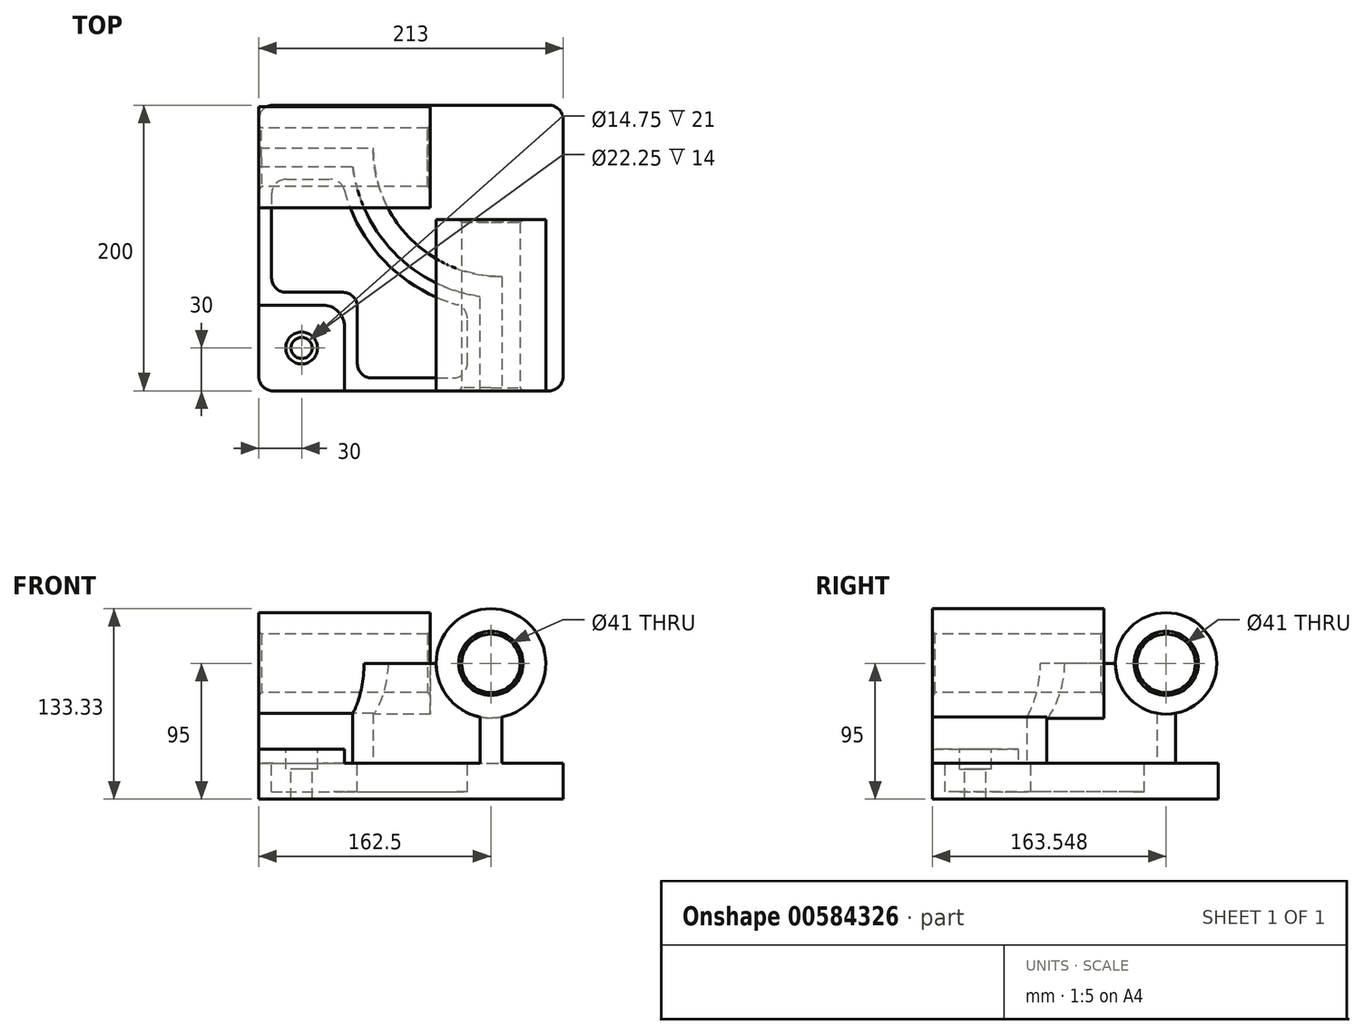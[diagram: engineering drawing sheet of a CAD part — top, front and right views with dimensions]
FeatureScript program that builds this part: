
annotation { "Feature Type Name" : "Feature", "Feature Type Description" : "" }
export const myFeature = defineFeature(function(context is Context, id is Id, definition is map)
    precondition{}
    {
        {
            var Q0;
            Q0=qCreatedBy(makeId("Top.planeOp"),FACE);
            var sketch = newSketch(context, id + "F0", { "sketchPlane" : qUnion([Q0])});
            skLineSegment(sketch, "E0.bottom", {"start": v(-106.5, 100) * mm, "end": v(106.5, 100) * mm});
            skLineSegment(sketch, "E0.top", {"start": v(-106.5, -100) * mm, "end": v(106.5, -100) * mm});
            skLineSegment(sketch, "E0.left", {"start": v(-106.5, 100) * mm, "end": v(-106.5, -100) * mm});
            skLineSegment(sketch, "E0.right", {"start": v(106.5, 100) * mm, "end": v(106.5, -100) * mm});
            skPoint(sketch, "E0.middle", {"position": v(0, 0) * mm});
            skSolve(sketch);
        }
        {
            var Q0;
            Q0 = qSketchRegion(id + "F0", true);
            extrude(context, id + "F1", {"entities" : qUnion([Q0]), "depth" : 25 * mm, "offsetDistance" : 25 * mm});
        }
        {
            var Q0;
            Q0=makeQuery(id+"F1.opExtrude","CAP_FACE",FACE,{"disambiguationData":[OSD([sQuery(id+"F0.wireOp",EDGE,"E0.bottom"),sQuery(id+"F0.wireOp",EDGE,"E0.top"),sQuery(id+"F0.wireOp",EDGE,"E0.left"),sQuery(id+"F0.wireOp",EDGE,"E0.right")])],"isStart":false});
            var sketch = newSketch(context, id + "F2", { "sketchPlane" : qUnion([Q0])});
            skLineSegment(sketch, "E1.bottom", {"start": v(-106.5, -100) * mm, "end": v(-46.5, -100) * mm});
            skLineSegment(sketch, "E1.top", {"start": v(-106.5, -40) * mm, "end": v(-46.5, -40) * mm});
            skLineSegment(sketch, "E1.left", {"start": v(-106.5, -100) * mm, "end": v(-106.5, -40) * mm});
            skLineSegment(sketch, "E1.right", {"start": v(-46.5, -100) * mm, "end": v(-46.5, -40) * mm});
            skLineSegment(sketch, "E2", {"start": v(-97.5, 48.1) * mm, "end": v(-97.5, -31) * mm});
            skLineSegment(sketch, "E3", {"start": v(-97.5, -31) * mm, "end": v(-37.5, -31) * mm});
            skLineSegment(sketch, "E4", {"start": v(-37.5, -31) * mm, "end": v(-37.5, -91) * mm});
            skLineSegment(sketch, "E5", {"start": v(-37.5, -91) * mm, "end": v(39.5, -91) * mm});
            skLineSegment(sketch, "E6", {"start": v(-97.5, 48.1) * mm, "end": v(-48.38, 48.1) * mm});
            skLineSegment(sketch, "E7", {"start": v(-106.5, 57.1) * mm, "end": v(-40.7, 57.1) * mm});
            skLineSegment(sketch, "E8", {"start": v(-106.5, 70) * mm, "end": v(-26.5, 70) * mm});
            skLineSegment(sketch, "E9", {"start": v(-26.5, 70) * mm, "end": v(63.5, 70) * mm, "construction": true});
            skLineSegment(sketch, "E10", {"start": v(63.5, 70) * mm, "end": v(63.5, -20) * mm, "construction": true});
            skPoint(sketch, "E11", {"position": v(63.5, -20) * mm});
            skPoint(sketch, "E12", {"position": v(-26.5, 70) * mm});
            skLineSegment(sketch, "E13.0", {"start": v(106.5, 100) * mm, "end": v(106.5, -100) * mm});
            skLineSegment(sketch, "E14", {"start": v(93.5, -100) * mm, "end": v(93.5, 100) * mm});
            skArc(sketch, "E15", {"start": v(-26.5, 70) * mm, "mid": v(-0.14, 6.36) * mm, "end": v(63.5, -20) * mm});
            skArc(sketch, "E16", {"start": v(-40.7, 57.1) * mm, "mid": v(-11.5, -3.5) * mm, "end": v(48.5, -33.92) * mm});
            skLineSegment(sketch, "E17", {"start": v(63.5, -20) * mm, "end": v(63.5, -100) * mm});
            skPoint(sketch, "E18", {"position": v(-40.7, 57.1) * mm});
            skLineSegment(sketch, "E19", {"start": v(39.5, -91) * mm, "end": v(39.5, -41.45) * mm});
            skPoint(sketch, "E20", {"position": v(-48.38, 48.1) * mm});
            skPoint(sketch, "E21", {"position": v(39.5, -41.45) * mm});
            skArc(sketch, "E22.trimOffspring", {"start": v(-48.38, 48.1) * mm, "mid": v(-17.86, -9.85) * mm, "end": v(39.5, -41.45) * mm});
            skLineSegment(sketch, "E23", {"start": v(48.5, -100) * mm, "end": v(48.5, -33.92) * mm});
            skSolve(sketch);
        }
        {
            var Q0;
            Q0=makeQuery(id+"F2.imprint","IMPRINT",FACE,{"disambiguationData":[TD([[makeQuery(id+"F2.imprint","IMPRINT",EDGE,{"derivedFrom":sQuery(id+"F2.wireOp",EDGE,"E1.bottom")}),1.0]])]});
            extrude(context, id + "F3", {"entities" : qUnion([Q0]), "operationType" : NewBodyOperationType.ADD, "depth" : 10 * mm, "offsetDistance" : 25 * mm});
        }
        {
            var Q0;
            Q0=makeQuery(id+"F3.boolean.opBoolean","MERGE",EDGE,{"derivedFrom":[makeQuery(id+"F1.opExtrude","SWEPT_EDGE",EDGE,{"disambiguationData":[OSD([sQuery(id+"F0.wireOp",EDGE,"E0.top"),sQuery(id+"F0.wireOp",EDGE,"E0.left")])]}),makeQuery(id+"F3.opExtrude","SWEPT_EDGE",EDGE,{"disambiguationData":[OSD([sQuery(id+"F2.wireOp",EDGE,"E1.bottom"),sQuery(id+"F2.wireOp",EDGE,"E1.left")])]})]});
            var Q1;
            Q1=makeQuery(id+"F1.opExtrude","SWEPT_EDGE",EDGE,{"disambiguationData":[OSD([sQuery(id+"F0.wireOp",EDGE,"E0.top"),sQuery(id+"F0.wireOp",EDGE,"E0.right")])]});
            var Q2;
            Q2=makeQuery(id+"F1.opExtrude","SWEPT_EDGE",EDGE,{"disambiguationData":[OSD([sQuery(id+"F0.wireOp",EDGE,"E0.bottom"),sQuery(id+"F0.wireOp",EDGE,"E0.right")])]});
            var Q3;
            Q3=makeQuery(id+"F1.opExtrude","SWEPT_EDGE",EDGE,{"disambiguationData":[OSD([sQuery(id+"F0.wireOp",EDGE,"E0.bottom"),sQuery(id+"F0.wireOp",EDGE,"E0.left")])]});
            fillet(context, id + "F4", {"entities" : qUnion([Q0, Q1, Q2, Q3]), "radius" : 10 * mm, "tangentPropagation" : true, "allowEdgeOverflow" : false});
        }
        {
            var Q0;
            Q0=makeQuery(id+"F3.opExtrude","SWEPT_EDGE",EDGE,{"disambiguationData":[OSD([sQuery(id+"F2.wireOp",EDGE,"E1.top"),sQuery(id+"F2.wireOp",EDGE,"E1.right")])]});
            fillet(context, id + "F5", {"entities" : qUnion([Q0]), "radius" : 15 * mm, "tangentPropagation" : true, "allowEdgeOverflow" : false});
        }
        {
            var Q0;
            Q0=makeQuery(id+"F2.imprint","IMPRINT",FACE,{"disambiguationData":[TD([[makeQuery(id+"F2.imprint","IMPRINT",EDGE,{"derivedFrom":sQuery(id+"F2.wireOp",EDGE,"E2")}),1.0]])]});
            extrude(context, id + "F6", {"entities" : qUnion([Q0]), "operationType" : NewBodyOperationType.REMOVE, "oppositeDirection" : true, "depth" : 20 * mm, "offsetDistance" : 25 * mm});
        }
        {
            var Q0;
            {var subQ4=sQuery(id+"F2.wireOp",EDGE,"E7");Q0=makeQuery(id+"F2.imprint","IMPRINT",FACE,{"disambiguationData":[TD([[makeQuery(id+"F2.imprint","IMPRINT",EDGE,{"derivedFrom":subQ4}),1.0]])]});}
            extrude(context, id + "F7", {"entities" : qUnion([Q0]), "operationType" : NewBodyOperationType.ADD, "depth" : 70 * mm, "offsetDistance" : 25 * mm});
        }
        {
            var Q0;
            Q0=makeQuery(id+"F6.boolean.opBoolean","COPY",EDGE,{"derivedFrom":makeQuery(id+"F6.opExtrude","SWEPT_EDGE",EDGE,{"disambiguationData":[OSD([sQuery(id+"F2.wireOp",EDGE,"E6"),sQuery(id+"F2.wireOp",EDGE,"E22.trimOffspring")])]})});
            var Q1;
            Q1=makeQuery(id+"F6.boolean.opBoolean","COPY",EDGE,{"derivedFrom":makeQuery(id+"F6.opExtrude","SWEPT_EDGE",EDGE,{"disambiguationData":[OSD([sQuery(id+"F2.wireOp",EDGE,"E19"),sQuery(id+"F2.wireOp",EDGE,"E22.trimOffspring")])]})});
            var Q2;
            Q2=makeQuery(id+"F6.boolean.opBoolean","COPY",EDGE,{"derivedFrom":makeQuery(id+"F6.opExtrude","SWEPT_EDGE",EDGE,{"disambiguationData":[OSD([sQuery(id+"F2.wireOp",EDGE,"E3"),sQuery(id+"F2.wireOp",EDGE,"E4")])]})});
            var Q3;
            Q3=makeQuery(id+"F6.boolean.opBoolean","COPY",EDGE,{"derivedFrom":makeQuery(id+"F6.opExtrude","SWEPT_EDGE",EDGE,{"disambiguationData":[OSD([sQuery(id+"F2.wireOp",EDGE,"E2"),sQuery(id+"F2.wireOp",EDGE,"E6")])]})});
            var Q4;
            Q4=makeQuery(id+"F6.boolean.opBoolean","COPY",EDGE,{"derivedFrom":makeQuery(id+"F6.opExtrude","SWEPT_EDGE",EDGE,{"disambiguationData":[OSD([sQuery(id+"F2.wireOp",EDGE,"E5"),sQuery(id+"F2.wireOp",EDGE,"E19")])]})});
            var Q5;
            Q5=makeQuery(id+"F6.boolean.opBoolean","COPY",EDGE,{"derivedFrom":makeQuery(id+"F6.opExtrude","SWEPT_EDGE",EDGE,{"disambiguationData":[OSD([sQuery(id+"F2.wireOp",EDGE,"E4"),sQuery(id+"F2.wireOp",EDGE,"E5")])]})});
            var Q6;
            Q6=makeQuery(id+"F6.boolean.opBoolean","COPY",EDGE,{"derivedFrom":makeQuery(id+"F6.opExtrude","SWEPT_EDGE",EDGE,{"disambiguationData":[OSD([sQuery(id+"F2.wireOp",EDGE,"E2"),sQuery(id+"F2.wireOp",EDGE,"E3")])]})});
            fillet(context, id + "F8", {"entities" : qUnion([Q0, Q1, Q2, Q3, Q4, Q5, Q6]), "radius" : 10 * mm, "tangentPropagation" : true, "allowEdgeOverflow" : false});
        }
        {
            var Q0;
            Q0=makeQuery(id+"F7.opExtrude","SWEPT_FACE",FACE,{"disambiguationData":[OSD([sQuery(id+"F0.wireOp",EDGE,"E0.left")])]});
            var sketch = newSketch(context, id + "F9", { "sketchPlane" : qUnion([Q0])});
            skCircle(sketch, "E24", {"center": v(-63.55, 95) * mm, "radius": 35.5 * mm});
            skCircle(sketch, "E25", {"center": v(-63.55, 95) * mm, "radius": 20.5 * mm});
            skSolve(sketch);
        }
        {
            var Q0;
            {var subQ1=sQuery(id+"F0.wireOp",EDGE,"E0.left");var subQ6=makeQuery(id+"F7.opExtrude","CAP_EDGE",EDGE,{"disambiguationData":[OSD([subQ1])],"isStart":false});Q0=makeQuery(id+"F9.imprint","IMPRINT",FACE,{"disambiguationData":[TD([[makeQuery(id+"F9.imprint","IMPRINT",EDGE,{"derivedFrom":subQ6}),1.0]])]});}
            var Q1;
            {var subQ1=sQuery(id+"F0.wireOp",EDGE,"E0.left");var subQ6=makeQuery(id+"F7.opExtrude","CAP_EDGE",EDGE,{"disambiguationData":[OSD([subQ1])],"isStart":false});Q1=makeQuery(id+"F9.imprint","IMPRINT",FACE,{"disambiguationData":[TD([[makeQuery(id+"F9.imprint","IMPRINT",EDGE,{"derivedFrom":subQ6}),-1.0]])]});}
            var Q2;
            {var subQ0=sQuery(id+"F9.wireOp",EDGE,"E24");var subQ1=sQuery(id+"F0.wireOp",EDGE,"E0.left");var subQ2=makeQuery(id+"F7.opExtrude","SWEPT_EDGE",EDGE,{"disambiguationData":[OSD([subQ1,sQuery(id+"F2.wireOp",EDGE,"E7")])]});var subQ3=makeQuery(id+"F9.imprint","INTERSECT",VERTEX,{"derivedFrom":[subQ2,subQ0]});Q2=makeQuery(id+"F9.imprint","IMPRINT",FACE,{"disambiguationData":[TD([[makeQuery(id+"F9.imprint","IMPRINT",EDGE,{"disambiguationData":[TD([[subQ3,-1.0]])],"derivedFrom":subQ0}),1.0]])]});}
            extrude(context, id + "F10", {"entities" : qUnion([Q0, Q1, Q2]), "operationType" : NewBodyOperationType.REMOVE, "oppositeDirection" : true, "depth" : 120 * mm, "offsetDistance" : 25 * mm});
        }
        {
            var Q0;
            {var subQ0=sQuery(id+"F9.wireOp",EDGE,"E24");var subQ1=sQuery(id+"F0.wireOp",EDGE,"E0.left");var subQ2=makeQuery(id+"F7.opExtrude","SWEPT_EDGE",EDGE,{"disambiguationData":[OSD([subQ1,sQuery(id+"F2.wireOp",EDGE,"E7")])]});var subQ3=makeQuery(id+"F9.imprint","INTERSECT",VERTEX,{"derivedFrom":[subQ2,subQ0]});Q0=makeQuery(id+"F9.imprint","IMPRINT",FACE,{"disambiguationData":[TD([[makeQuery(id+"F9.imprint","IMPRINT",EDGE,{"disambiguationData":[TD([[subQ3,-1.0]])],"derivedFrom":subQ0}),1.0]])]});}
            var Q1;
            {var subQ0=sQuery(id+"F9.wireOp",EDGE,"E24");var subQ1=sQuery(id+"F0.wireOp",EDGE,"E0.left");var subQ2=makeQuery(id+"F7.opExtrude","SWEPT_EDGE",EDGE,{"disambiguationData":[OSD([subQ1,sQuery(id+"F2.wireOp",EDGE,"E7")])]});var subQ3=makeQuery(id+"F9.imprint","INTERSECT",VERTEX,{"derivedFrom":[subQ2,subQ0]});Q1=makeQuery(id+"F9.imprint","IMPRINT",FACE,{"disambiguationData":[TD([[makeQuery(id+"F9.imprint","IMPRINT",EDGE,{"disambiguationData":[TD([[subQ3,1.0]])],"derivedFrom":subQ0}),1.0]])]});}
            extrude(context, id + "F11", {"entities" : qUnion([Q0, Q1]), "operationType" : NewBodyOperationType.ADD, "oppositeDirection" : true, "depth" : 120 * mm, "offsetDistance" : 25 * mm});
        }
        {
            var Q0;
            {var subQ0=sQuery(id+"F9.wireOp",EDGE,"E25");Q0=makeQuery(id+"F11.boolean.opBoolean","MERGE",EDGE,{"derivedFrom":[makeQuery(id+"F10.boolean.opBoolean","COPY",EDGE,{"derivedFrom":makeQuery(id+"F10.opExtrude","CAP_EDGE",EDGE,{"disambiguationData":[OSD([subQ0])],"isStart":true})}),makeQuery(id+"F11.opExtrude","CAP_EDGE",EDGE,{"disambiguationData":[OSD([subQ0])],"isStart":true})]});}
            chamfer(context, id + "F12", {"entities" : qUnion([Q0]), "width" : 2 * mm, "tangentPropagation" : true});
        }
        {
            var Q0;
            Q0=makeQuery(id+"F7.opExtrude","SWEPT_FACE",FACE,{"disambiguationData":[OSD([sQuery(id+"F0.wireOp",EDGE,"E0.top")])]});
            var sketch = newSketch(context, id + "F13", { "sketchPlane" : qUnion([Q0])});
            skCircle(sketch, "E26", {"center": v(56, 95) * mm, "radius": 38.33 * mm});
            skCircle(sketch, "E27", {"center": v(56, 95) * mm, "radius": 20.5 * mm});
            skSolve(sketch);
        }
        {
            var Q0;
            {var subQ1=sQuery(id+"F0.wireOp",EDGE,"E0.top");var subQ6=makeQuery(id+"F7.opExtrude","CAP_EDGE",EDGE,{"disambiguationData":[OSD([subQ1])],"isStart":false});Q0=makeQuery(id+"F13.imprint","IMPRINT",FACE,{"disambiguationData":[TD([[makeQuery(id+"F13.imprint","IMPRINT",EDGE,{"derivedFrom":subQ6}),1.0]])]});}
            var Q1;
            {var subQ1=sQuery(id+"F0.wireOp",EDGE,"E0.top");var subQ6=makeQuery(id+"F7.opExtrude","CAP_EDGE",EDGE,{"disambiguationData":[OSD([subQ1])],"isStart":false});Q1=makeQuery(id+"F13.imprint","IMPRINT",FACE,{"disambiguationData":[TD([[makeQuery(id+"F13.imprint","IMPRINT",EDGE,{"derivedFrom":subQ6}),-1.0]])]});}
            extrude(context, id + "F14", {"entities" : qUnion([Q0, Q1]), "operationType" : NewBodyOperationType.REMOVE, "oppositeDirection" : true, "depth" : 120 * mm, "offsetDistance" : 25 * mm});
        }
        {
            var Q0;
            {var subQ0=sQuery(id+"F13.wireOp",EDGE,"E26");var subQ1=sQuery(id+"F0.wireOp",EDGE,"E0.top");var subQ2=makeQuery(id+"F7.opExtrude","SWEPT_EDGE",EDGE,{"disambiguationData":[OSD([subQ1,sQuery(id+"F2.wireOp",EDGE,"E17")])]});var subQ3=makeQuery(id+"F13.imprint","INTERSECT",VERTEX,{"derivedFrom":[subQ2,subQ0]});Q0=makeQuery(id+"F13.imprint","IMPRINT",FACE,{"disambiguationData":[TD([[makeQuery(id+"F13.imprint","IMPRINT",EDGE,{"disambiguationData":[TD([[subQ3,-1.0]])],"derivedFrom":subQ0}),1.0]])]});}
            var Q1;
            {var subQ0=sQuery(id+"F13.wireOp",EDGE,"E26");var subQ1=sQuery(id+"F0.wireOp",EDGE,"E0.top");var subQ2=makeQuery(id+"F7.opExtrude","SWEPT_EDGE",EDGE,{"disambiguationData":[OSD([subQ1,sQuery(id+"F2.wireOp",EDGE,"E17")])]});var subQ3=makeQuery(id+"F13.imprint","INTERSECT",VERTEX,{"derivedFrom":[subQ2,subQ0]});Q1=makeQuery(id+"F13.imprint","IMPRINT",FACE,{"disambiguationData":[TD([[makeQuery(id+"F13.imprint","IMPRINT",EDGE,{"disambiguationData":[TD([[subQ3,1.0]])],"derivedFrom":subQ0}),1.0]])]});}
            extrude(context, id + "F15", {"entities" : qUnion([Q0, Q1]), "operationType" : NewBodyOperationType.ADD, "oppositeDirection" : true, "depth" : 120 * mm, "offsetDistance" : 25 * mm});
        }
        {
            var Q0;
            {var subQ0=sQuery(id+"F13.wireOp",EDGE,"E27");Q0=makeQuery(id+"F15.boolean.opBoolean","MERGE",EDGE,{"derivedFrom":[makeQuery(id+"F14.boolean.opBoolean","COPY",EDGE,{"derivedFrom":makeQuery(id+"F14.opExtrude","CAP_EDGE",EDGE,{"disambiguationData":[OSD([subQ0])],"isStart":true})}),makeQuery(id+"F15.opExtrude","CAP_EDGE",EDGE,{"disambiguationData":[OSD([subQ0])],"isStart":true})]});}
            chamfer(context, id + "F16", {"entities" : qUnion([Q0]), "width" : 2 * mm, "tangentPropagation" : true});
        }
        {
            var Q0;
            Q0=makeQuery(id+"F3.opExtrude","CAP_FACE",FACE,{"disambiguationData":[OSD([sQuery(id+"F2.wireOp",EDGE,"E1.bottom"),sQuery(id+"F2.wireOp",EDGE,"E1.top"),sQuery(id+"F2.wireOp",EDGE,"E1.left"),sQuery(id+"F2.wireOp",EDGE,"E1.right")])],"isStart":false});
            var sketch = newSketch(context, id + "F17", { "sketchPlane" : qUnion([Q0])});
            skLineSegment(sketch, "E28", {"start": v(-106.5, -40) * mm, "end": v(-46.5, -100) * mm, "construction": true});
            skLineSegment(sketch, "E29", {"start": v(-103.57, -97.07) * mm, "end": v(-50.9, -44.4) * mm, "construction": true});
            skPoint(sketch, "E29.startSnap0", {"position": v(-103.57, -97.07) * mm});
            skPoint(sketch, "E30", {"position": v(-76.5, -70) * mm});
            skSolve(sketch);
        }
        {
            var Q0;
            Q0=sQuery(id+"F17.wireOp",VERTEX,"E30");
            var Q1;
            Q1=makeQuery(id+"F1.opExtrude","SWEPT_BODY",BODY,{"disambiguationData":[OSD([sQuery(id+"F0.wireOp",EDGE,"E0.bottom"),sQuery(id+"F0.wireOp",EDGE,"E0.top"),sQuery(id+"F0.wireOp",EDGE,"E0.left"),sQuery(id+"F0.wireOp",EDGE,"E0.right")])]});
            hole(context, id + "F18", {"style" : HoleStyle.C_BORE, "endStyle" : HoleEndStyle.THROUGH, "standardTappedOrClearance" : lookupTablePath({ "standard" : "ISO", "fit" : "Close", "size" : "M14", "type" : "Clearance" }), "standardBlindInLast" : lookupTablePath({ "fit" : "Close", "standard" : "ISO", "size" : "M14", "type" : "Clearance" }), "holeDiameter" : 14.75 * mm, "cBoreDiameter" : 22.25 * mm, "cBoreDepth" : 14 * mm, "majorDiameter" : 14 * mm, "isTappedThrough" : true, "tappedDepth" : 12 * mm, "tapClearance" : 3, "locations" : qUnion([Q0]), "scope" : qUnion([Q1])});
        }
        {
            var Q0;
            Q0=makeQuery(id+"F15.opExtrude","CAP_EDGE",EDGE,{"disambiguationData":[OSD([sQuery(id+"F13.wireOp",EDGE,"E27")])],"isStart":false});
            chamfer(context, id + "F19", {"entities" : qUnion([Q0]), "width" : 2 * mm, "tangentPropagation" : true});
        }
        {
            var Q0;
            Q0=makeQuery(id+"F11.opExtrude","CAP_EDGE",EDGE,{"disambiguationData":[OSD([sQuery(id+"F9.wireOp",EDGE,"E25")])],"isStart":false});
            chamfer(context, id + "F20", {"entities" : qUnion([Q0]), "width" : 2 * mm, "tangentPropagation" : true});
        }
    });
